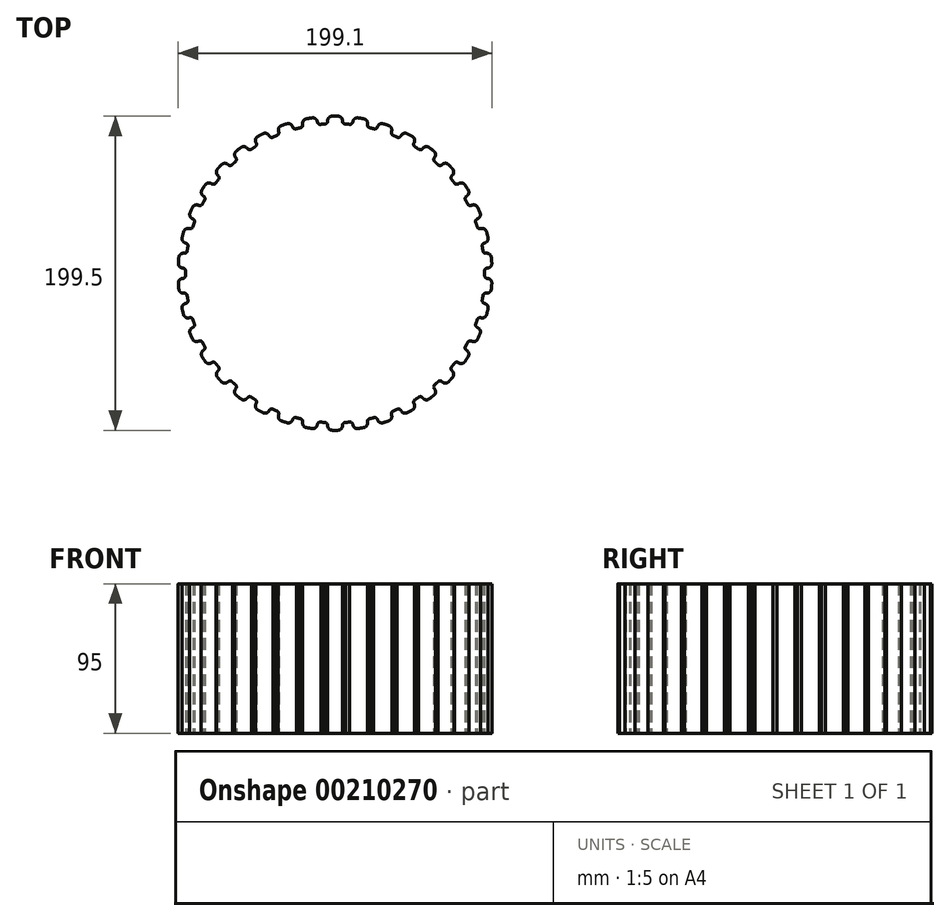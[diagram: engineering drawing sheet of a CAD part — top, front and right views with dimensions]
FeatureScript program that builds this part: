
annotation { "Feature Type Name" : "Feature", "Feature Type Description" : "" }
export const myFeature = defineFeature(function(context is Context, id is Id, definition is map)
    precondition{}
    {
        {
            var Q0;
            Q0=qCreatedBy(makeId("Top.planeOp"),FACE);
            var sketch = newSketch(context, id + "F0", { "sketchPlane" : qUnion([Q0])});
            skLineSegment(sketch, "E0", {"start": v(0, 0) * mm, "end": v(0, 110) * mm, "construction": true});
            skArc(sketch, "E1", {"start": v(2, 104.98) * mm, "mid": v(0, 105) * mm, "end": v(-2, 104.98) * mm});
            skArc(sketch, "E2.filletArc", {"start": v(-2, 104.98) * mm, "mid": v(-4.13, 104.03) * mm, "end": v(-4.94, 101.85) * mm});
            skArc(sketch, "E3.filletArc", {"start": v(4.94, 101.85) * mm, "mid": v(4.13, 104.03) * mm, "end": v(2, 104.98) * mm});
            skArc(sketch, "E4", {"start": v(-6.98, 99.76) * mm, "mid": v(-5.5, 100.36) * mm, "end": v(-4.94, 101.85) * mm});
            skLineSegment(sketch, "E5", {"start": v(-6.98, 99.76) * mm, "end": v(0, 0) * mm, "construction": true});
            skLineSegment(sketch, "E6", {"start": v(0, 0) * mm, "end": v(6.98, 99.76) * mm, "construction": true});
            skCircle(sketch, "E7", {"center": v(0, 0) * mm, "radius": 100 * mm});
            skArc(sketch, "E8", {"start": v(4.94, 101.85) * mm, "mid": v(5.5, 100.36) * mm, "end": v(6.98, 99.76) * mm});
            skArc(sketch, "E9.1.0", {"start": v(-23.3, 97.25) * mm, "mid": v(-21.95, 98.09) * mm, "end": v(-21.64, 99.64) * mm});
            skArc(sketch, "E9.1.1", {"start": v(-19.25, 103.22) * mm, "mid": v(-21.2, 101.93) * mm, "end": v(-21.64, 99.64) * mm});
            skArc(sketch, "E9.1.2", {"start": v(-15.3, 103.88) * mm, "mid": v(-17.28, 103.57) * mm, "end": v(-19.25, 103.22) * mm});
            skArc(sketch, "E9.1.3", {"start": v(-11.9, 101.27) * mm, "mid": v(-13.05, 103.3) * mm, "end": v(-15.3, 103.88) * mm});
            skArc(sketch, "E9.1.4", {"start": v(-11.9, 101.27) * mm, "mid": v(-11.09, 99.9) * mm, "end": v(-9.54, 99.54) * mm});
            skArc(sketch, "E9.2.0", {"start": v(-38.99, 92.09) * mm, "mid": v(-37.8, 93.14) * mm, "end": v(-37.74, 94.72) * mm});
            skArc(sketch, "E9.2.1", {"start": v(-35.98, 98.64) * mm, "mid": v(-37.69, 97.06) * mm, "end": v(-37.74, 94.72) * mm});
            skArc(sketch, "E9.2.2", {"start": v(-32.2, 99.94) * mm, "mid": v(-34.1, 99.31) * mm, "end": v(-35.98, 98.64) * mm});
            skArc(sketch, "E9.2.3", {"start": v(-28.4, 97.93) * mm, "mid": v(-29.87, 99.74) * mm, "end": v(-32.2, 99.94) * mm});
            skArc(sketch, "E9.2.4", {"start": v(-28.4, 97.93) * mm, "mid": v(-27.38, 96.71) * mm, "end": v(-25.8, 96.62) * mm});
            skArc(sketch, "E9.3.0", {"start": v(-53.61, 84.41) * mm, "mid": v(-52.6, 85.64) * mm, "end": v(-52.82, 87.22) * mm});
            skArc(sketch, "E9.3.1", {"start": v(-51.72, 91.38) * mm, "mid": v(-53.15, 89.53) * mm, "end": v(-52.82, 87.22) * mm});
            skArc(sketch, "E9.3.2", {"start": v(-48.2, 93.28) * mm, "mid": v(-49.97, 92.34) * mm, "end": v(-51.72, 91.38) * mm});
            skArc(sketch, "E9.3.3", {"start": v(-44.13, 91.92) * mm, "mid": v(-45.88, 93.46) * mm, "end": v(-48.2, 93.28) * mm});
            skArc(sketch, "E9.3.4", {"start": v(-44.13, 91.92) * mm, "mid": v(-42.92, 90.88) * mm, "end": v(-41.34, 91.05) * mm});
            skArc(sketch, "E9.4.0", {"start": v(-66.78, 74.44) * mm, "mid": v(-65.99, 75.82) * mm, "end": v(-66.45, 77.34) * mm});
            skArc(sketch, "E9.4.1", {"start": v(-66.06, 81.62) * mm, "mid": v(-67.16, 79.56) * mm, "end": v(-66.45, 77.34) * mm});
            skArc(sketch, "E9.4.2", {"start": v(-62.9, 84.07) * mm, "mid": v(-64.5, 82.86) * mm, "end": v(-66.06, 81.62) * mm});
            skArc(sketch, "E9.4.3", {"start": v(-58.66, 83.4) * mm, "mid": v(-60.64, 84.63) * mm, "end": v(-62.9, 84.07) * mm});
            skArc(sketch, "E9.4.4", {"start": v(-58.66, 83.4) * mm, "mid": v(-57.3, 82.58) * mm, "end": v(-55.77, 83) * mm});
            skArc(sketch, "E9.5.0", {"start": v(-78.12, 62.43) * mm, "mid": v(-77.57, 63.92) * mm, "end": v(-78.28, 65.34) * mm});
            skArc(sketch, "E9.5.1", {"start": v(-78.6, 69.63) * mm, "mid": v(-79.34, 67.42) * mm, "end": v(-78.28, 65.34) * mm});
            skArc(sketch, "E9.5.2", {"start": v(-75.88, 72.57) * mm, "mid": v(-77.25, 71.11) * mm, "end": v(-78.6, 69.63) * mm});
            skArc(sketch, "E9.5.3", {"start": v(-71.59, 72.61) * mm, "mid": v(-73.74, 73.5) * mm, "end": v(-75.88, 72.57) * mm});
            skArc(sketch, "E9.5.4", {"start": v(-71.59, 72.61) * mm, "mid": v(-70.1, 72.02) * mm, "end": v(-68.67, 72.7) * mm});
            skArc(sketch, "E9.6.0", {"start": v(-87.33, 48.72) * mm, "mid": v(-87.03, 50.28) * mm, "end": v(-87.96, 51.57) * mm});
            skArc(sketch, "E9.6.1", {"start": v(-88.98, 55.74) * mm, "mid": v(-89.35, 53.44) * mm, "end": v(-87.96, 51.57) * mm});
            skArc(sketch, "E9.6.2", {"start": v(-86.8, 59.1) * mm, "mid": v(-87.9, 57.43) * mm, "end": v(-88.98, 55.74) * mm});
            skArc(sketch, "E9.6.3", {"start": v(-82.56, 59.84) * mm, "mid": v(-84.83, 60.36) * mm, "end": v(-86.8, 59.1) * mm});
            skArc(sketch, "E9.6.4", {"start": v(-82.56, 59.84) * mm, "mid": v(-81, 59.5) * mm, "end": v(-79.7, 60.4) * mm});
            skArc(sketch, "E9.7.0", {"start": v(-94.16, 33.68) * mm, "mid": v(-94.12, 35.27) * mm, "end": v(-95.25, 36.39) * mm});
            skArc(sketch, "E9.7.1", {"start": v(-96.94, 40.34) * mm, "mid": v(-96.93, 38) * mm, "end": v(-95.25, 36.39) * mm});
            skArc(sketch, "E9.7.2", {"start": v(-95.34, 44) * mm, "mid": v(-96.16, 42.18) * mm, "end": v(-96.94, 40.34) * mm});
            skArc(sketch, "E9.7.3", {"start": v(-91.28, 45.43) * mm, "mid": v(-93.61, 45.57) * mm, "end": v(-95.34, 44) * mm});
            skArc(sketch, "E9.7.4", {"start": v(-91.28, 45.43) * mm, "mid": v(-89.7, 45.36) * mm, "end": v(-88.55, 46.46) * mm});
            skArc(sketch, "E9.8.0", {"start": v(-98.42, 17.73) * mm, "mid": v(-98.64, 19.3) * mm, "end": v(-99.94, 20.21) * mm});
            skArc(sketch, "E9.8.1", {"start": v(-102.26, 23.83) * mm, "mid": v(-101.86, 21.53) * mm, "end": v(-99.94, 20.21) * mm});
            skArc(sketch, "E9.8.2", {"start": v(-101.28, 27.71) * mm, "mid": v(-101.79, 25.78) * mm, "end": v(-102.26, 23.83) * mm});
            skArc(sketch, "E9.8.3", {"start": v(-97.52, 29.8) * mm, "mid": v(-99.84, 29.54) * mm, "end": v(-101.28, 27.71) * mm});
            skArc(sketch, "E9.8.4", {"start": v(-97.52, 29.8) * mm, "mid": v(-95.94, 29.97) * mm, "end": v(-95, 31.25) * mm});
            skArc(sketch, "E9.9.0", {"start": v(-100, 1.29) * mm, "mid": v(-100.47, 2.8) * mm, "end": v(-101.9, 3.49) * mm});
            skArc(sketch, "E9.9.1", {"start": v(-104.79, 6.68) * mm, "mid": v(-104.02, 4.47) * mm, "end": v(-101.9, 3.49) * mm});
            skArc(sketch, "E9.9.2", {"start": v(-104.46, 10.66) * mm, "mid": v(-104.64, 8.67) * mm, "end": v(-104.79, 6.68) * mm});
            skArc(sketch, "E9.9.3", {"start": v(-101.1, 13.33) * mm, "mid": v(-103.34, 12.7) * mm, "end": v(-104.46, 10.66) * mm});
            skArc(sketch, "E9.9.4", {"start": v(-101.1, 13.33) * mm, "mid": v(-99.56, 13.77) * mm, "end": v(-98.84, 15.19) * mm});
            skArc(sketch, "E9.10.0", {"start": v(-98.84, -15.19) * mm, "mid": v(-99.56, -13.77) * mm, "end": v(-101.1, -13.33) * mm});
            skArc(sketch, "E9.10.1", {"start": v(-104.46, -10.66) * mm, "mid": v(-103.34, -12.7) * mm, "end": v(-101.1, -13.33) * mm});
            skArc(sketch, "E9.10.2", {"start": v(-104.79, -6.68) * mm, "mid": v(-104.64, -8.67) * mm, "end": v(-104.46, -10.66) * mm});
            skArc(sketch, "E9.10.3", {"start": v(-101.9, -3.49) * mm, "mid": v(-104.02, -4.47) * mm, "end": v(-104.79, -6.68) * mm});
            skArc(sketch, "E9.10.4", {"start": v(-101.9, -3.49) * mm, "mid": v(-100.47, -2.8) * mm, "end": v(-100, -1.29) * mm});
            skArc(sketch, "E9.11.0", {"start": v(-95, -31.25) * mm, "mid": v(-95.94, -29.97) * mm, "end": v(-97.52, -29.8) * mm});
            skArc(sketch, "E9.11.1", {"start": v(-101.28, -27.71) * mm, "mid": v(-99.84, -29.54) * mm, "end": v(-97.52, -29.8) * mm});
            skArc(sketch, "E9.11.2", {"start": v(-102.26, -23.83) * mm, "mid": v(-101.79, -25.78) * mm, "end": v(-101.28, -27.71) * mm});
            skArc(sketch, "E9.11.3", {"start": v(-99.94, -20.21) * mm, "mid": v(-101.86, -21.53) * mm, "end": v(-102.26, -23.83) * mm});
            skArc(sketch, "E9.11.4", {"start": v(-99.94, -20.21) * mm, "mid": v(-98.64, -19.3) * mm, "end": v(-98.42, -17.73) * mm});
            skArc(sketch, "E9.12.0", {"start": v(-88.55, -46.46) * mm, "mid": v(-89.7, -45.36) * mm, "end": v(-91.28, -45.43) * mm});
            skArc(sketch, "E9.12.1", {"start": v(-95.34, -44) * mm, "mid": v(-93.61, -45.57) * mm, "end": v(-91.28, -45.43) * mm});
            skArc(sketch, "E9.12.2", {"start": v(-96.94, -40.34) * mm, "mid": v(-96.16, -42.18) * mm, "end": v(-95.34, -44) * mm});
            skArc(sketch, "E9.12.3", {"start": v(-95.25, -36.39) * mm, "mid": v(-96.93, -38) * mm, "end": v(-96.94, -40.34) * mm});
            skArc(sketch, "E9.12.4", {"start": v(-95.25, -36.39) * mm, "mid": v(-94.12, -35.27) * mm, "end": v(-94.16, -33.68) * mm});
            skArc(sketch, "E9.13.0", {"start": v(-79.7, -60.4) * mm, "mid": v(-81, -59.5) * mm, "end": v(-82.56, -59.84) * mm});
            skArc(sketch, "E9.13.1", {"start": v(-86.8, -59.1) * mm, "mid": v(-84.83, -60.36) * mm, "end": v(-82.56, -59.84) * mm});
            skArc(sketch, "E9.13.2", {"start": v(-88.98, -55.74) * mm, "mid": v(-87.9, -57.43) * mm, "end": v(-86.8, -59.1) * mm});
            skArc(sketch, "E9.13.3", {"start": v(-87.96, -51.57) * mm, "mid": v(-89.35, -53.44) * mm, "end": v(-88.98, -55.74) * mm});
            skArc(sketch, "E9.13.4", {"start": v(-87.96, -51.57) * mm, "mid": v(-87.03, -50.28) * mm, "end": v(-87.33, -48.72) * mm});
            skArc(sketch, "E9.14.0", {"start": v(-68.67, -72.7) * mm, "mid": v(-70.1, -72.02) * mm, "end": v(-71.59, -72.61) * mm});
            skArc(sketch, "E9.14.1", {"start": v(-75.88, -72.57) * mm, "mid": v(-73.74, -73.5) * mm, "end": v(-71.59, -72.61) * mm});
            skArc(sketch, "E9.14.2", {"start": v(-78.6, -69.63) * mm, "mid": v(-77.25, -71.11) * mm, "end": v(-75.88, -72.57) * mm});
            skArc(sketch, "E9.14.3", {"start": v(-78.28, -65.34) * mm, "mid": v(-79.34, -67.42) * mm, "end": v(-78.6, -69.63) * mm});
            skArc(sketch, "E9.14.4", {"start": v(-78.28, -65.34) * mm, "mid": v(-77.57, -63.92) * mm, "end": v(-78.12, -62.43) * mm});
            skArc(sketch, "E9.15.0", {"start": v(-55.77, -83) * mm, "mid": v(-57.3, -82.58) * mm, "end": v(-58.66, -83.4) * mm});
            skArc(sketch, "E9.15.1", {"start": v(-62.9, -84.07) * mm, "mid": v(-60.64, -84.63) * mm, "end": v(-58.66, -83.4) * mm});
            skArc(sketch, "E9.15.2", {"start": v(-66.06, -81.62) * mm, "mid": v(-64.5, -82.86) * mm, "end": v(-62.9, -84.07) * mm});
            skArc(sketch, "E9.15.3", {"start": v(-66.45, -77.34) * mm, "mid": v(-67.16, -79.56) * mm, "end": v(-66.06, -81.62) * mm});
            skArc(sketch, "E9.15.4", {"start": v(-66.45, -77.34) * mm, "mid": v(-65.99, -75.82) * mm, "end": v(-66.78, -74.44) * mm});
            skArc(sketch, "E9.16.0", {"start": v(-41.34, -91.05) * mm, "mid": v(-42.92, -90.88) * mm, "end": v(-44.13, -91.92) * mm});
            skArc(sketch, "E9.16.1", {"start": v(-48.2, -93.28) * mm, "mid": v(-45.88, -93.46) * mm, "end": v(-44.13, -91.92) * mm});
            skArc(sketch, "E9.16.2", {"start": v(-51.72, -91.38) * mm, "mid": v(-49.97, -92.34) * mm, "end": v(-48.2, -93.28) * mm});
            skArc(sketch, "E9.16.3", {"start": v(-52.82, -87.22) * mm, "mid": v(-53.15, -89.53) * mm, "end": v(-51.72, -91.38) * mm});
            skArc(sketch, "E9.16.4", {"start": v(-52.82, -87.22) * mm, "mid": v(-52.6, -85.64) * mm, "end": v(-53.61, -84.41) * mm});
            skArc(sketch, "E9.17.0", {"start": v(-25.8, -96.62) * mm, "mid": v(-27.38, -96.71) * mm, "end": v(-28.4, -97.93) * mm});
            skArc(sketch, "E9.17.1", {"start": v(-32.2, -99.94) * mm, "mid": v(-29.87, -99.74) * mm, "end": v(-28.4, -97.93) * mm});
            skArc(sketch, "E9.17.2", {"start": v(-35.98, -98.64) * mm, "mid": v(-34.1, -99.31) * mm, "end": v(-32.2, -99.94) * mm});
            skArc(sketch, "E9.17.3", {"start": v(-37.74, -94.72) * mm, "mid": v(-37.69, -97.06) * mm, "end": v(-35.98, -98.64) * mm});
            skArc(sketch, "E9.17.4", {"start": v(-37.74, -94.72) * mm, "mid": v(-37.8, -93.14) * mm, "end": v(-38.99, -92.09) * mm});
            skArc(sketch, "E9.18.0", {"start": v(-9.54, -99.54) * mm, "mid": v(-11.09, -99.9) * mm, "end": v(-11.9, -101.27) * mm});
            skArc(sketch, "E9.18.1", {"start": v(-15.3, -103.88) * mm, "mid": v(-13.05, -103.3) * mm, "end": v(-11.9, -101.27) * mm});
            skArc(sketch, "E9.18.2", {"start": v(-19.25, -103.22) * mm, "mid": v(-17.28, -103.57) * mm, "end": v(-15.3, -103.88) * mm});
            skArc(sketch, "E9.18.3", {"start": v(-21.64, -99.64) * mm, "mid": v(-21.2, -101.93) * mm, "end": v(-19.25, -103.22) * mm});
            skArc(sketch, "E9.18.4", {"start": v(-21.64, -99.64) * mm, "mid": v(-21.95, -98.09) * mm, "end": v(-23.3, -97.25) * mm});
            skArc(sketch, "E9.19.0", {"start": v(6.98, -99.76) * mm, "mid": v(5.5, -100.36) * mm, "end": v(4.94, -101.85) * mm});
            skArc(sketch, "E9.19.1", {"start": v(2, -104.98) * mm, "mid": v(4.13, -104.03) * mm, "end": v(4.94, -101.85) * mm});
            skArc(sketch, "E9.19.2", {"start": v(-2, -104.98) * mm, "mid": v(0, -105) * mm, "end": v(2, -104.98) * mm});
            skArc(sketch, "E9.19.3", {"start": v(-4.94, -101.85) * mm, "mid": v(-4.13, -104.03) * mm, "end": v(-2, -104.98) * mm});
            skArc(sketch, "E9.19.4", {"start": v(-4.94, -101.85) * mm, "mid": v(-5.5, -100.36) * mm, "end": v(-6.98, -99.76) * mm});
            skArc(sketch, "E9.20.0", {"start": v(23.3, -97.25) * mm, "mid": v(21.95, -98.09) * mm, "end": v(21.64, -99.64) * mm});
            skArc(sketch, "E9.20.1", {"start": v(19.25, -103.22) * mm, "mid": v(21.2, -101.93) * mm, "end": v(21.64, -99.64) * mm});
            skArc(sketch, "E9.20.2", {"start": v(15.3, -103.88) * mm, "mid": v(17.28, -103.57) * mm, "end": v(19.25, -103.22) * mm});
            skArc(sketch, "E9.20.3", {"start": v(11.9, -101.27) * mm, "mid": v(13.05, -103.3) * mm, "end": v(15.3, -103.88) * mm});
            skArc(sketch, "E9.20.4", {"start": v(11.9, -101.27) * mm, "mid": v(11.09, -99.9) * mm, "end": v(9.54, -99.54) * mm});
            skArc(sketch, "E9.21.0", {"start": v(38.99, -92.09) * mm, "mid": v(37.8, -93.14) * mm, "end": v(37.74, -94.72) * mm});
            skArc(sketch, "E9.21.1", {"start": v(35.98, -98.64) * mm, "mid": v(37.69, -97.06) * mm, "end": v(37.74, -94.72) * mm});
            skArc(sketch, "E9.21.2", {"start": v(32.2, -99.94) * mm, "mid": v(34.1, -99.31) * mm, "end": v(35.98, -98.64) * mm});
            skArc(sketch, "E9.21.3", {"start": v(28.4, -97.93) * mm, "mid": v(29.87, -99.74) * mm, "end": v(32.2, -99.94) * mm});
            skArc(sketch, "E9.21.4", {"start": v(28.4, -97.93) * mm, "mid": v(27.38, -96.71) * mm, "end": v(25.8, -96.62) * mm});
            skArc(sketch, "E9.22.0", {"start": v(53.61, -84.41) * mm, "mid": v(52.6, -85.64) * mm, "end": v(52.82, -87.22) * mm});
            skArc(sketch, "E9.22.1", {"start": v(51.72, -91.38) * mm, "mid": v(53.15, -89.53) * mm, "end": v(52.82, -87.22) * mm});
            skArc(sketch, "E9.22.2", {"start": v(48.2, -93.28) * mm, "mid": v(49.97, -92.34) * mm, "end": v(51.72, -91.38) * mm});
            skArc(sketch, "E9.22.3", {"start": v(44.13, -91.92) * mm, "mid": v(45.88, -93.46) * mm, "end": v(48.2, -93.28) * mm});
            skArc(sketch, "E9.22.4", {"start": v(44.13, -91.92) * mm, "mid": v(42.92, -90.88) * mm, "end": v(41.34, -91.05) * mm});
            skArc(sketch, "E9.23.0", {"start": v(66.78, -74.44) * mm, "mid": v(65.99, -75.82) * mm, "end": v(66.45, -77.34) * mm});
            skArc(sketch, "E9.23.1", {"start": v(66.06, -81.62) * mm, "mid": v(67.16, -79.56) * mm, "end": v(66.45, -77.34) * mm});
            skArc(sketch, "E9.23.2", {"start": v(62.9, -84.07) * mm, "mid": v(64.5, -82.86) * mm, "end": v(66.06, -81.62) * mm});
            skArc(sketch, "E9.23.3", {"start": v(58.66, -83.4) * mm, "mid": v(60.64, -84.63) * mm, "end": v(62.9, -84.07) * mm});
            skArc(sketch, "E9.23.4", {"start": v(58.66, -83.4) * mm, "mid": v(57.3, -82.58) * mm, "end": v(55.77, -83) * mm});
            skArc(sketch, "E9.24.0", {"start": v(78.12, -62.43) * mm, "mid": v(77.57, -63.92) * mm, "end": v(78.28, -65.34) * mm});
            skArc(sketch, "E9.24.1", {"start": v(78.6, -69.63) * mm, "mid": v(79.34, -67.42) * mm, "end": v(78.28, -65.34) * mm});
            skArc(sketch, "E9.24.2", {"start": v(75.88, -72.57) * mm, "mid": v(77.25, -71.11) * mm, "end": v(78.6, -69.63) * mm});
            skArc(sketch, "E9.24.3", {"start": v(71.59, -72.61) * mm, "mid": v(73.74, -73.5) * mm, "end": v(75.88, -72.57) * mm});
            skArc(sketch, "E9.24.4", {"start": v(71.59, -72.61) * mm, "mid": v(70.1, -72.02) * mm, "end": v(68.67, -72.7) * mm});
            skArc(sketch, "E9.25.0", {"start": v(87.33, -48.72) * mm, "mid": v(87.03, -50.28) * mm, "end": v(87.96, -51.57) * mm});
            skArc(sketch, "E9.25.1", {"start": v(88.98, -55.74) * mm, "mid": v(89.35, -53.44) * mm, "end": v(87.96, -51.57) * mm});
            skArc(sketch, "E9.25.2", {"start": v(86.8, -59.1) * mm, "mid": v(87.9, -57.43) * mm, "end": v(88.98, -55.74) * mm});
            skArc(sketch, "E9.25.3", {"start": v(82.56, -59.84) * mm, "mid": v(84.83, -60.36) * mm, "end": v(86.8, -59.1) * mm});
            skArc(sketch, "E9.25.4", {"start": v(82.56, -59.84) * mm, "mid": v(81, -59.5) * mm, "end": v(79.7, -60.4) * mm});
            skArc(sketch, "E9.26.0", {"start": v(94.16, -33.68) * mm, "mid": v(94.12, -35.27) * mm, "end": v(95.25, -36.39) * mm});
            skArc(sketch, "E9.26.1", {"start": v(96.94, -40.34) * mm, "mid": v(96.93, -38) * mm, "end": v(95.25, -36.39) * mm});
            skArc(sketch, "E9.26.2", {"start": v(95.34, -44) * mm, "mid": v(96.16, -42.18) * mm, "end": v(96.94, -40.34) * mm});
            skArc(sketch, "E9.26.3", {"start": v(91.28, -45.43) * mm, "mid": v(93.61, -45.57) * mm, "end": v(95.34, -44) * mm});
            skArc(sketch, "E9.26.4", {"start": v(91.28, -45.43) * mm, "mid": v(89.7, -45.36) * mm, "end": v(88.55, -46.46) * mm});
            skArc(sketch, "E9.27.0", {"start": v(98.42, -17.73) * mm, "mid": v(98.64, -19.3) * mm, "end": v(99.94, -20.21) * mm});
            skArc(sketch, "E9.27.1", {"start": v(102.26, -23.83) * mm, "mid": v(101.86, -21.53) * mm, "end": v(99.94, -20.21) * mm});
            skArc(sketch, "E9.27.2", {"start": v(101.28, -27.71) * mm, "mid": v(101.79, -25.78) * mm, "end": v(102.26, -23.83) * mm});
            skArc(sketch, "E9.27.3", {"start": v(97.52, -29.8) * mm, "mid": v(99.84, -29.54) * mm, "end": v(101.28, -27.71) * mm});
            skArc(sketch, "E9.27.4", {"start": v(97.52, -29.8) * mm, "mid": v(95.94, -29.97) * mm, "end": v(95, -31.25) * mm});
            skArc(sketch, "E9.28.0", {"start": v(100, -1.29) * mm, "mid": v(100.47, -2.8) * mm, "end": v(101.9, -3.49) * mm});
            skArc(sketch, "E9.28.1", {"start": v(104.79, -6.68) * mm, "mid": v(104.02, -4.47) * mm, "end": v(101.9, -3.49) * mm});
            skArc(sketch, "E9.28.2", {"start": v(104.46, -10.66) * mm, "mid": v(104.64, -8.67) * mm, "end": v(104.79, -6.68) * mm});
            skArc(sketch, "E9.28.3", {"start": v(101.1, -13.33) * mm, "mid": v(103.34, -12.7) * mm, "end": v(104.46, -10.66) * mm});
            skArc(sketch, "E9.28.4", {"start": v(101.1, -13.33) * mm, "mid": v(99.56, -13.77) * mm, "end": v(98.84, -15.19) * mm});
            skArc(sketch, "E9.29.0", {"start": v(98.84, 15.19) * mm, "mid": v(99.56, 13.77) * mm, "end": v(101.1, 13.33) * mm});
            skArc(sketch, "E9.29.1", {"start": v(104.46, 10.66) * mm, "mid": v(103.34, 12.7) * mm, "end": v(101.1, 13.33) * mm});
            skArc(sketch, "E9.29.2", {"start": v(104.79, 6.68) * mm, "mid": v(104.64, 8.67) * mm, "end": v(104.46, 10.66) * mm});
            skArc(sketch, "E9.29.3", {"start": v(101.9, 3.49) * mm, "mid": v(104.02, 4.47) * mm, "end": v(104.79, 6.68) * mm});
            skArc(sketch, "E9.29.4", {"start": v(101.9, 3.49) * mm, "mid": v(100.47, 2.8) * mm, "end": v(100, 1.29) * mm});
            skArc(sketch, "E9.30.0", {"start": v(95, 31.25) * mm, "mid": v(95.94, 29.97) * mm, "end": v(97.52, 29.8) * mm});
            skArc(sketch, "E9.30.1", {"start": v(101.28, 27.71) * mm, "mid": v(99.84, 29.54) * mm, "end": v(97.52, 29.8) * mm});
            skArc(sketch, "E9.30.2", {"start": v(102.26, 23.83) * mm, "mid": v(101.79, 25.78) * mm, "end": v(101.28, 27.71) * mm});
            skArc(sketch, "E9.30.3", {"start": v(99.94, 20.21) * mm, "mid": v(101.86, 21.53) * mm, "end": v(102.26, 23.83) * mm});
            skArc(sketch, "E9.30.4", {"start": v(99.94, 20.21) * mm, "mid": v(98.64, 19.3) * mm, "end": v(98.42, 17.73) * mm});
            skArc(sketch, "E9.31.0", {"start": v(88.55, 46.46) * mm, "mid": v(89.7, 45.36) * mm, "end": v(91.28, 45.43) * mm});
            skArc(sketch, "E9.31.1", {"start": v(95.34, 44) * mm, "mid": v(93.61, 45.57) * mm, "end": v(91.28, 45.43) * mm});
            skArc(sketch, "E9.31.2", {"start": v(96.94, 40.34) * mm, "mid": v(96.16, 42.18) * mm, "end": v(95.34, 44) * mm});
            skArc(sketch, "E9.31.3", {"start": v(95.25, 36.39) * mm, "mid": v(96.93, 38) * mm, "end": v(96.94, 40.34) * mm});
            skArc(sketch, "E9.31.4", {"start": v(95.25, 36.39) * mm, "mid": v(94.12, 35.27) * mm, "end": v(94.16, 33.68) * mm});
            skArc(sketch, "E9.32.0", {"start": v(79.7, 60.4) * mm, "mid": v(81, 59.5) * mm, "end": v(82.56, 59.84) * mm});
            skArc(sketch, "E9.32.1", {"start": v(86.8, 59.1) * mm, "mid": v(84.83, 60.36) * mm, "end": v(82.56, 59.84) * mm});
            skArc(sketch, "E9.32.2", {"start": v(88.98, 55.74) * mm, "mid": v(87.9, 57.43) * mm, "end": v(86.8, 59.1) * mm});
            skArc(sketch, "E9.32.3", {"start": v(87.96, 51.57) * mm, "mid": v(89.35, 53.44) * mm, "end": v(88.98, 55.74) * mm});
            skArc(sketch, "E9.32.4", {"start": v(87.96, 51.57) * mm, "mid": v(87.03, 50.28) * mm, "end": v(87.33, 48.72) * mm});
            skArc(sketch, "E9.33.0", {"start": v(68.67, 72.7) * mm, "mid": v(70.1, 72.02) * mm, "end": v(71.59, 72.61) * mm});
            skArc(sketch, "E9.33.1", {"start": v(75.88, 72.57) * mm, "mid": v(73.74, 73.5) * mm, "end": v(71.59, 72.61) * mm});
            skArc(sketch, "E9.33.2", {"start": v(78.6, 69.63) * mm, "mid": v(77.25, 71.11) * mm, "end": v(75.88, 72.57) * mm});
            skArc(sketch, "E9.33.3", {"start": v(78.28, 65.34) * mm, "mid": v(79.34, 67.42) * mm, "end": v(78.6, 69.63) * mm});
            skArc(sketch, "E9.33.4", {"start": v(78.28, 65.34) * mm, "mid": v(77.57, 63.92) * mm, "end": v(78.12, 62.43) * mm});
            skArc(sketch, "E9.34.0", {"start": v(55.77, 83) * mm, "mid": v(57.3, 82.58) * mm, "end": v(58.66, 83.4) * mm});
            skArc(sketch, "E9.34.1", {"start": v(62.9, 84.07) * mm, "mid": v(60.64, 84.63) * mm, "end": v(58.66, 83.4) * mm});
            skArc(sketch, "E9.34.2", {"start": v(66.06, 81.62) * mm, "mid": v(64.5, 82.86) * mm, "end": v(62.9, 84.07) * mm});
            skArc(sketch, "E9.34.3", {"start": v(66.45, 77.34) * mm, "mid": v(67.16, 79.56) * mm, "end": v(66.06, 81.62) * mm});
            skArc(sketch, "E9.34.4", {"start": v(66.45, 77.34) * mm, "mid": v(65.99, 75.82) * mm, "end": v(66.78, 74.44) * mm});
            skArc(sketch, "E9.35.0", {"start": v(41.34, 91.05) * mm, "mid": v(42.92, 90.88) * mm, "end": v(44.13, 91.92) * mm});
            skArc(sketch, "E9.35.1", {"start": v(48.2, 93.28) * mm, "mid": v(45.88, 93.46) * mm, "end": v(44.13, 91.92) * mm});
            skArc(sketch, "E9.35.2", {"start": v(51.72, 91.38) * mm, "mid": v(49.97, 92.34) * mm, "end": v(48.2, 93.28) * mm});
            skArc(sketch, "E9.35.3", {"start": v(52.82, 87.22) * mm, "mid": v(53.15, 89.53) * mm, "end": v(51.72, 91.38) * mm});
            skArc(sketch, "E9.35.4", {"start": v(52.82, 87.22) * mm, "mid": v(52.6, 85.64) * mm, "end": v(53.61, 84.41) * mm});
            skArc(sketch, "E9.36.0", {"start": v(25.8, 96.62) * mm, "mid": v(27.38, 96.71) * mm, "end": v(28.4, 97.93) * mm});
            skArc(sketch, "E9.36.1", {"start": v(32.2, 99.94) * mm, "mid": v(29.87, 99.74) * mm, "end": v(28.4, 97.93) * mm});
            skArc(sketch, "E9.36.2", {"start": v(35.98, 98.64) * mm, "mid": v(34.1, 99.31) * mm, "end": v(32.2, 99.94) * mm});
            skArc(sketch, "E9.36.3", {"start": v(37.74, 94.72) * mm, "mid": v(37.69, 97.06) * mm, "end": v(35.98, 98.64) * mm});
            skArc(sketch, "E9.36.4", {"start": v(37.74, 94.72) * mm, "mid": v(37.8, 93.14) * mm, "end": v(38.99, 92.09) * mm});
            skArc(sketch, "E9.37.0", {"start": v(9.54, 99.54) * mm, "mid": v(11.09, 99.9) * mm, "end": v(11.9, 101.27) * mm});
            skArc(sketch, "E9.37.1", {"start": v(15.3, 103.88) * mm, "mid": v(13.05, 103.3) * mm, "end": v(11.9, 101.27) * mm});
            skArc(sketch, "E9.37.2", {"start": v(19.25, 103.22) * mm, "mid": v(17.28, 103.57) * mm, "end": v(15.3, 103.88) * mm});
            skArc(sketch, "E9.37.3", {"start": v(21.64, 99.64) * mm, "mid": v(21.2, 101.93) * mm, "end": v(19.25, 103.22) * mm});
            skArc(sketch, "E9.37.4", {"start": v(21.64, 99.64) * mm, "mid": v(21.95, 98.09) * mm, "end": v(23.3, 97.25) * mm});
            skSolve(sketch);
        }
        {
            var Q0;
            {var subQ0=sQuery(id+"F0.wireOp",EDGE,"E9.3.1");Q0=makeQuery(id+"F0.imprint","IMPRINT",FACE,{"disambiguationData":[TD([[makeQuery(id+"F0.imprint","IMPRINT",EDGE,{"derivedFrom":subQ0}),1.0]])]});}
            var Q1;
            {var subQ0=sQuery(id+"F0.wireOp",EDGE,"E9.2.1");Q1=makeQuery(id+"F0.imprint","IMPRINT",FACE,{"disambiguationData":[TD([[makeQuery(id+"F0.imprint","IMPRINT",EDGE,{"derivedFrom":subQ0}),1.0]])]});}
            var Q2;
            {var subQ0=sQuery(id+"F0.wireOp",EDGE,"E9.1.1");Q2=makeQuery(id+"F0.imprint","IMPRINT",FACE,{"disambiguationData":[TD([[makeQuery(id+"F0.imprint","IMPRINT",EDGE,{"derivedFrom":subQ0}),1.0]])]});}
            var Q3;
            Q3=makeQuery(id+"F0.imprint","IMPRINT",FACE,{"disambiguationData":[TD([[makeQuery(id+"F0.imprint","IMPRINT",EDGE,{"derivedFrom":sQuery(id+"F0.wireOp",EDGE,"E1")}),1.0]])]});
            var Q4;
            {var subQ1=sQuery(id+"F0.wireOp",EDGE,"E9.37.1");Q4=makeQuery(id+"F0.imprint","IMPRINT",FACE,{"disambiguationData":[TD([[makeQuery(id+"F0.imprint","IMPRINT",EDGE,{"derivedFrom":subQ1}),1.0]])]});}
            var Q5;
            {var subQ0=sQuery(id+"F0.wireOp",EDGE,"E9.36.1");Q5=makeQuery(id+"F0.imprint","IMPRINT",FACE,{"disambiguationData":[TD([[makeQuery(id+"F0.imprint","IMPRINT",EDGE,{"derivedFrom":subQ0}),1.0]])]});}
            var Q6;
            {var subQ0=sQuery(id+"F0.wireOp",EDGE,"E9.35.1");Q6=makeQuery(id+"F0.imprint","IMPRINT",FACE,{"disambiguationData":[TD([[makeQuery(id+"F0.imprint","IMPRINT",EDGE,{"derivedFrom":subQ0}),1.0]])]});}
            var Q7;
            {var subQ0=sQuery(id+"F0.wireOp",EDGE,"E9.34.1");Q7=makeQuery(id+"F0.imprint","IMPRINT",FACE,{"disambiguationData":[TD([[makeQuery(id+"F0.imprint","IMPRINT",EDGE,{"derivedFrom":subQ0}),1.0]])]});}
            var Q8;
            {var subQ0=sQuery(id+"F0.wireOp",EDGE,"E9.33.1");Q8=makeQuery(id+"F0.imprint","IMPRINT",FACE,{"disambiguationData":[TD([[makeQuery(id+"F0.imprint","IMPRINT",EDGE,{"derivedFrom":subQ0}),1.0]])]});}
            var Q9;
            {var subQ0=sQuery(id+"F0.wireOp",EDGE,"E9.32.1");Q9=makeQuery(id+"F0.imprint","IMPRINT",FACE,{"disambiguationData":[TD([[makeQuery(id+"F0.imprint","IMPRINT",EDGE,{"derivedFrom":subQ0}),1.0]])]});}
            var Q10;
            {var subQ0=sQuery(id+"F0.wireOp",EDGE,"E9.31.1");Q10=makeQuery(id+"F0.imprint","IMPRINT",FACE,{"disambiguationData":[TD([[makeQuery(id+"F0.imprint","IMPRINT",EDGE,{"derivedFrom":subQ0}),1.0]])]});}
            var Q11;
            {var subQ5=sQuery(id+"F0.wireOp",EDGE,"E9.30.1");Q11=makeQuery(id+"F0.imprint","IMPRINT",FACE,{"disambiguationData":[TD([[makeQuery(id+"F0.imprint","IMPRINT",EDGE,{"derivedFrom":subQ5}),1.0]])]});}
            var Q12;
            {var subQ5=sQuery(id+"F0.wireOp",EDGE,"E9.4.1");Q12=makeQuery(id+"F0.imprint","IMPRINT",FACE,{"disambiguationData":[TD([[makeQuery(id+"F0.imprint","IMPRINT",EDGE,{"derivedFrom":subQ5}),1.0]])]});}
            var Q13;
            {var subQ0=sQuery(id+"F0.wireOp",EDGE,"E9.5.1");Q13=makeQuery(id+"F0.imprint","IMPRINT",FACE,{"disambiguationData":[TD([[makeQuery(id+"F0.imprint","IMPRINT",EDGE,{"derivedFrom":subQ0}),1.0]])]});}
            var Q14;
            {var subQ0=sQuery(id+"F0.wireOp",EDGE,"E9.6.1");Q14=makeQuery(id+"F0.imprint","IMPRINT",FACE,{"disambiguationData":[TD([[makeQuery(id+"F0.imprint","IMPRINT",EDGE,{"derivedFrom":subQ0}),1.0]])]});}
            var Q15;
            {var subQ0=sQuery(id+"F0.wireOp",EDGE,"E9.7.1");Q15=makeQuery(id+"F0.imprint","IMPRINT",FACE,{"disambiguationData":[TD([[makeQuery(id+"F0.imprint","IMPRINT",EDGE,{"derivedFrom":subQ0}),1.0]])]});}
            var Q16;
            {var subQ0=sQuery(id+"F0.wireOp",EDGE,"E9.8.1");Q16=makeQuery(id+"F0.imprint","IMPRINT",FACE,{"disambiguationData":[TD([[makeQuery(id+"F0.imprint","IMPRINT",EDGE,{"derivedFrom":subQ0}),1.0]])]});}
            var Q17;
            {var subQ1=sQuery(id+"F0.wireOp",EDGE,"E9.9.1");Q17=makeQuery(id+"F0.imprint","IMPRINT",FACE,{"disambiguationData":[TD([[makeQuery(id+"F0.imprint","IMPRINT",EDGE,{"derivedFrom":subQ1}),1.0]])]});}
            var Q18;
            {var subQ0=sQuery(id+"F0.wireOp",EDGE,"E9.10.1");Q18=makeQuery(id+"F0.imprint","IMPRINT",FACE,{"disambiguationData":[TD([[makeQuery(id+"F0.imprint","IMPRINT",EDGE,{"derivedFrom":subQ0}),1.0]])]});}
            var Q19;
            {var subQ0=sQuery(id+"F0.wireOp",EDGE,"E9.11.1");Q19=makeQuery(id+"F0.imprint","IMPRINT",FACE,{"disambiguationData":[TD([[makeQuery(id+"F0.imprint","IMPRINT",EDGE,{"derivedFrom":subQ0}),1.0]])]});}
            var Q20;
            {var subQ0=sQuery(id+"F0.wireOp",EDGE,"E9.12.1");Q20=makeQuery(id+"F0.imprint","IMPRINT",FACE,{"disambiguationData":[TD([[makeQuery(id+"F0.imprint","IMPRINT",EDGE,{"derivedFrom":subQ0}),1.0]])]});}
            var Q21;
            {var subQ0=sQuery(id+"F0.wireOp",EDGE,"E9.13.1");Q21=makeQuery(id+"F0.imprint","IMPRINT",FACE,{"disambiguationData":[TD([[makeQuery(id+"F0.imprint","IMPRINT",EDGE,{"derivedFrom":subQ0}),1.0]])]});}
            var Q22;
            {var subQ0=sQuery(id+"F0.wireOp",EDGE,"E9.14.1");Q22=makeQuery(id+"F0.imprint","IMPRINT",FACE,{"disambiguationData":[TD([[makeQuery(id+"F0.imprint","IMPRINT",EDGE,{"derivedFrom":subQ0}),1.0]])]});}
            var Q23;
            {var subQ0=sQuery(id+"F0.wireOp",EDGE,"E9.15.1");Q23=makeQuery(id+"F0.imprint","IMPRINT",FACE,{"disambiguationData":[TD([[makeQuery(id+"F0.imprint","IMPRINT",EDGE,{"derivedFrom":subQ0}),1.0]])]});}
            var Q24;
            {var subQ0=sQuery(id+"F0.wireOp",EDGE,"E9.16.1");Q24=makeQuery(id+"F0.imprint","IMPRINT",FACE,{"disambiguationData":[TD([[makeQuery(id+"F0.imprint","IMPRINT",EDGE,{"derivedFrom":subQ0}),1.0]])]});}
            var Q25;
            {var subQ0=sQuery(id+"F0.wireOp",EDGE,"E9.17.1");Q25=makeQuery(id+"F0.imprint","IMPRINT",FACE,{"disambiguationData":[TD([[makeQuery(id+"F0.imprint","IMPRINT",EDGE,{"derivedFrom":subQ0}),1.0]])]});}
            var Q26;
            {var subQ0=sQuery(id+"F0.wireOp",EDGE,"E9.18.1");Q26=makeQuery(id+"F0.imprint","IMPRINT",FACE,{"disambiguationData":[TD([[makeQuery(id+"F0.imprint","IMPRINT",EDGE,{"derivedFrom":subQ0}),1.0]])]});}
            var Q27;
            {var subQ0=sQuery(id+"F0.wireOp",EDGE,"E9.19.1");Q27=makeQuery(id+"F0.imprint","IMPRINT",FACE,{"disambiguationData":[TD([[makeQuery(id+"F0.imprint","IMPRINT",EDGE,{"derivedFrom":subQ0}),1.0]])]});}
            var Q28;
            {var subQ0=sQuery(id+"F0.wireOp",EDGE,"E9.20.1");Q28=makeQuery(id+"F0.imprint","IMPRINT",FACE,{"disambiguationData":[TD([[makeQuery(id+"F0.imprint","IMPRINT",EDGE,{"derivedFrom":subQ0}),1.0]])]});}
            var Q29;
            {var subQ0=sQuery(id+"F0.wireOp",EDGE,"E9.21.1");Q29=makeQuery(id+"F0.imprint","IMPRINT",FACE,{"disambiguationData":[TD([[makeQuery(id+"F0.imprint","IMPRINT",EDGE,{"derivedFrom":subQ0}),1.0]])]});}
            var Q30;
            {var subQ0=sQuery(id+"F0.wireOp",EDGE,"E9.22.1");Q30=makeQuery(id+"F0.imprint","IMPRINT",FACE,{"disambiguationData":[TD([[makeQuery(id+"F0.imprint","IMPRINT",EDGE,{"derivedFrom":subQ0}),1.0]])]});}
            var Q31;
            {var subQ0=sQuery(id+"F0.wireOp",EDGE,"E9.23.1");Q31=makeQuery(id+"F0.imprint","IMPRINT",FACE,{"disambiguationData":[TD([[makeQuery(id+"F0.imprint","IMPRINT",EDGE,{"derivedFrom":subQ0}),1.0]])]});}
            var Q32;
            {var subQ1=sQuery(id+"F0.wireOp",EDGE,"E9.24.1");Q32=makeQuery(id+"F0.imprint","IMPRINT",FACE,{"disambiguationData":[TD([[makeQuery(id+"F0.imprint","IMPRINT",EDGE,{"derivedFrom":subQ1}),1.0]])]});}
            var Q33;
            {var subQ0=sQuery(id+"F0.wireOp",EDGE,"E9.25.1");Q33=makeQuery(id+"F0.imprint","IMPRINT",FACE,{"disambiguationData":[TD([[makeQuery(id+"F0.imprint","IMPRINT",EDGE,{"derivedFrom":subQ0}),1.0]])]});}
            var Q34;
            {var subQ0=sQuery(id+"F0.wireOp",EDGE,"E9.26.1");Q34=makeQuery(id+"F0.imprint","IMPRINT",FACE,{"disambiguationData":[TD([[makeQuery(id+"F0.imprint","IMPRINT",EDGE,{"derivedFrom":subQ0}),1.0]])]});}
            var Q35;
            {var subQ0=sQuery(id+"F0.wireOp",EDGE,"E9.27.1");Q35=makeQuery(id+"F0.imprint","IMPRINT",FACE,{"disambiguationData":[TD([[makeQuery(id+"F0.imprint","IMPRINT",EDGE,{"derivedFrom":subQ0}),1.0]])]});}
            var Q36;
            {var subQ0=sQuery(id+"F0.wireOp",EDGE,"E9.28.1");Q36=makeQuery(id+"F0.imprint","IMPRINT",FACE,{"disambiguationData":[TD([[makeQuery(id+"F0.imprint","IMPRINT",EDGE,{"derivedFrom":subQ0}),1.0]])]});}
            var Q37;
            {var subQ0=sQuery(id+"F0.wireOp",EDGE,"E9.29.1");Q37=makeQuery(id+"F0.imprint","IMPRINT",FACE,{"disambiguationData":[TD([[makeQuery(id+"F0.imprint","IMPRINT",EDGE,{"derivedFrom":subQ0}),1.0]])]});}
            var Q38;
            {var subQ1=sQuery(id+"F0.wireOp",EDGE,"E7");var subQ176=sQuery(id+"F0.wireOp",EDGE,"E4");var subQ177=makeQuery(id+"F0.imprint","INTERSECT",VERTEX,{"disambiguationData":[OD(0.0)],"derivedFrom":[subQ176,subQ1]});Q38=makeQuery(id+"F0.imprint","IMPRINT",FACE,{"disambiguationData":[TD([[makeQuery(id+"F0.imprint","IMPRINT",EDGE,{"disambiguationData":[TD([[subQ177,-1.0]])],"derivedFrom":subQ176}),-1.0]])]});}
            extrude(context, id + "F1", {"entities" : qUnion([Q0, Q1, Q2, Q3, Q4, Q5, Q6, Q7, Q8, Q9, Q10, Q11, Q12, Q13, Q14, Q15, Q16, Q17, Q18, Q19, Q20, Q21, Q22, Q23, Q24, Q25, Q26, Q27, Q28, Q29, Q30, Q31, Q32, Q33, Q34, Q35, Q36, Q37, Q38]), "depth" : 100 * mm});
        }
        {
            var Q0;
            Q0=makeQuery(id+"F1.opExtrude","SWEPT_BODY",BODY,{"disambiguationData":[OSD([sQuery(id+"F0.wireOp",EDGE,"E1"),sQuery(id+"F0.wireOp",EDGE,"E2.filletArc"),sQuery(id+"F0.wireOp",EDGE,"E3.filletArc"),sQuery(id+"F0.wireOp",EDGE,"E4"),sQuery(id+"F0.wireOp",EDGE,"E7"),sQuery(id+"F0.wireOp",EDGE,"E8"),sQuery(id+"F0.wireOp",EDGE,"E9.1.0"),sQuery(id+"F0.wireOp",EDGE,"E9.1.1"),sQuery(id+"F0.wireOp",EDGE,"E9.1.2"),sQuery(id+"F0.wireOp",EDGE,"E9.1.3"),sQuery(id+"F0.wireOp",EDGE,"E9.1.4"),sQuery(id+"F0.wireOp",EDGE,"E9.2.0"),sQuery(id+"F0.wireOp",EDGE,"E9.2.1"),sQuery(id+"F0.wireOp",EDGE,"E9.2.2"),sQuery(id+"F0.wireOp",EDGE,"E9.2.3"),sQuery(id+"F0.wireOp",EDGE,"E9.2.4"),sQuery(id+"F0.wireOp",EDGE,"E9.3.0"),sQuery(id+"F0.wireOp",EDGE,"E9.3.1"),sQuery(id+"F0.wireOp",EDGE,"E9.3.2"),sQuery(id+"F0.wireOp",EDGE,"E9.3.3"),sQuery(id+"F0.wireOp",EDGE,"E9.3.4"),sQuery(id+"F0.wireOp",EDGE,"E9.4.0"),sQuery(id+"F0.wireOp",EDGE,"E9.4.1"),sQuery(id+"F0.wireOp",EDGE,"E9.4.2"),sQuery(id+"F0.wireOp",EDGE,"E9.4.3"),sQuery(id+"F0.wireOp",EDGE,"E9.4.4"),sQuery(id+"F0.wireOp",EDGE,"E9.5.0"),sQuery(id+"F0.wireOp",EDGE,"E9.5.1"),sQuery(id+"F0.wireOp",EDGE,"E9.5.2"),sQuery(id+"F0.wireOp",EDGE,"E9.5.3"),sQuery(id+"F0.wireOp",EDGE,"E9.5.4"),sQuery(id+"F0.wireOp",EDGE,"E9.6.0"),sQuery(id+"F0.wireOp",EDGE,"E9.6.1"),sQuery(id+"F0.wireOp",EDGE,"E9.6.2"),sQuery(id+"F0.wireOp",EDGE,"E9.6.3"),sQuery(id+"F0.wireOp",EDGE,"E9.6.4"),sQuery(id+"F0.wireOp",EDGE,"E9.7.0"),sQuery(id+"F0.wireOp",EDGE,"E9.7.1"),sQuery(id+"F0.wireOp",EDGE,"E9.7.2"),sQuery(id+"F0.wireOp",EDGE,"E9.7.3"),sQuery(id+"F0.wireOp",EDGE,"E9.7.4"),sQuery(id+"F0.wireOp",EDGE,"E9.8.0"),sQuery(id+"F0.wireOp",EDGE,"E9.8.1"),sQuery(id+"F0.wireOp",EDGE,"E9.8.2"),sQuery(id+"F0.wireOp",EDGE,"E9.8.3"),sQuery(id+"F0.wireOp",EDGE,"E9.8.4"),sQuery(id+"F0.wireOp",EDGE,"E9.9.0"),sQuery(id+"F0.wireOp",EDGE,"E9.9.1"),sQuery(id+"F0.wireOp",EDGE,"E9.9.2"),sQuery(id+"F0.wireOp",EDGE,"E9.9.3"),sQuery(id+"F0.wireOp",EDGE,"E9.9.4"),sQuery(id+"F0.wireOp",EDGE,"E9.10.0"),sQuery(id+"F0.wireOp",EDGE,"E9.10.1"),sQuery(id+"F0.wireOp",EDGE,"E9.10.2"),sQuery(id+"F0.wireOp",EDGE,"E9.10.3"),sQuery(id+"F0.wireOp",EDGE,"E9.10.4"),sQuery(id+"F0.wireOp",EDGE,"E9.11.0"),sQuery(id+"F0.wireOp",EDGE,"E9.11.1"),sQuery(id+"F0.wireOp",EDGE,"E9.11.2"),sQuery(id+"F0.wireOp",EDGE,"E9.11.3"),sQuery(id+"F0.wireOp",EDGE,"E9.11.4"),sQuery(id+"F0.wireOp",EDGE,"E9.12.0"),sQuery(id+"F0.wireOp",EDGE,"E9.12.1"),sQuery(id+"F0.wireOp",EDGE,"E9.12.2"),sQuery(id+"F0.wireOp",EDGE,"E9.12.3"),sQuery(id+"F0.wireOp",EDGE,"E9.12.4"),sQuery(id+"F0.wireOp",EDGE,"E9.13.0"),sQuery(id+"F0.wireOp",EDGE,"E9.13.1"),sQuery(id+"F0.wireOp",EDGE,"E9.13.2"),sQuery(id+"F0.wireOp",EDGE,"E9.13.3"),sQuery(id+"F0.wireOp",EDGE,"E9.13.4"),sQuery(id+"F0.wireOp",EDGE,"E9.14.0"),sQuery(id+"F0.wireOp",EDGE,"E9.14.1"),sQuery(id+"F0.wireOp",EDGE,"E9.14.2"),sQuery(id+"F0.wireOp",EDGE,"E9.14.3"),sQuery(id+"F0.wireOp",EDGE,"E9.14.4"),sQuery(id+"F0.wireOp",EDGE,"E9.15.0"),sQuery(id+"F0.wireOp",EDGE,"E9.15.1"),sQuery(id+"F0.wireOp",EDGE,"E9.15.2"),sQuery(id+"F0.wireOp",EDGE,"E9.15.3"),sQuery(id+"F0.wireOp",EDGE,"E9.15.4"),sQuery(id+"F0.wireOp",EDGE,"E9.16.0"),sQuery(id+"F0.wireOp",EDGE,"E9.16.1"),sQuery(id+"F0.wireOp",EDGE,"E9.16.2"),sQuery(id+"F0.wireOp",EDGE,"E9.16.3"),sQuery(id+"F0.wireOp",EDGE,"E9.16.4"),sQuery(id+"F0.wireOp",EDGE,"E9.17.0"),sQuery(id+"F0.wireOp",EDGE,"E9.17.1"),sQuery(id+"F0.wireOp",EDGE,"E9.17.2"),sQuery(id+"F0.wireOp",EDGE,"E9.17.3"),sQuery(id+"F0.wireOp",EDGE,"E9.17.4"),sQuery(id+"F0.wireOp",EDGE,"E9.18.0"),sQuery(id+"F0.wireOp",EDGE,"E9.18.1"),sQuery(id+"F0.wireOp",EDGE,"E9.18.2"),sQuery(id+"F0.wireOp",EDGE,"E9.18.3"),sQuery(id+"F0.wireOp",EDGE,"E9.18.4"),sQuery(id+"F0.wireOp",EDGE,"E9.19.0"),sQuery(id+"F0.wireOp",EDGE,"E9.19.1"),sQuery(id+"F0.wireOp",EDGE,"E9.19.2"),sQuery(id+"F0.wireOp",EDGE,"E9.19.3"),sQuery(id+"F0.wireOp",EDGE,"E9.19.4"),sQuery(id+"F0.wireOp",EDGE,"E9.20.0"),sQuery(id+"F0.wireOp",EDGE,"E9.20.1"),sQuery(id+"F0.wireOp",EDGE,"E9.20.2"),sQuery(id+"F0.wireOp",EDGE,"E9.20.3"),sQuery(id+"F0.wireOp",EDGE,"E9.20.4"),sQuery(id+"F0.wireOp",EDGE,"E9.21.0"),sQuery(id+"F0.wireOp",EDGE,"E9.21.1"),sQuery(id+"F0.wireOp",EDGE,"E9.21.2"),sQuery(id+"F0.wireOp",EDGE,"E9.21.3"),sQuery(id+"F0.wireOp",EDGE,"E9.21.4"),sQuery(id+"F0.wireOp",EDGE,"E9.22.0"),sQuery(id+"F0.wireOp",EDGE,"E9.22.1"),sQuery(id+"F0.wireOp",EDGE,"E9.22.2"),sQuery(id+"F0.wireOp",EDGE,"E9.22.3"),sQuery(id+"F0.wireOp",EDGE,"E9.22.4"),sQuery(id+"F0.wireOp",EDGE,"E9.23.0"),sQuery(id+"F0.wireOp",EDGE,"E9.23.1"),sQuery(id+"F0.wireOp",EDGE,"E9.23.2"),sQuery(id+"F0.wireOp",EDGE,"E9.23.3"),sQuery(id+"F0.wireOp",EDGE,"E9.23.4"),sQuery(id+"F0.wireOp",EDGE,"E9.24.0"),sQuery(id+"F0.wireOp",EDGE,"E9.24.1"),sQuery(id+"F0.wireOp",EDGE,"E9.24.2"),sQuery(id+"F0.wireOp",EDGE,"E9.24.3"),sQuery(id+"F0.wireOp",EDGE,"E9.24.4"),sQuery(id+"F0.wireOp",EDGE,"E9.25.0"),sQuery(id+"F0.wireOp",EDGE,"E9.25.1"),sQuery(id+"F0.wireOp",EDGE,"E9.25.2"),sQuery(id+"F0.wireOp",EDGE,"E9.25.3"),sQuery(id+"F0.wireOp",EDGE,"E9.25.4"),sQuery(id+"F0.wireOp",EDGE,"E9.26.0"),sQuery(id+"F0.wireOp",EDGE,"E9.26.1"),sQuery(id+"F0.wireOp",EDGE,"E9.26.2"),sQuery(id+"F0.wireOp",EDGE,"E9.26.3"),sQuery(id+"F0.wireOp",EDGE,"E9.26.4"),sQuery(id+"F0.wireOp",EDGE,"E9.27.0"),sQuery(id+"F0.wireOp",EDGE,"E9.27.1"),sQuery(id+"F0.wireOp",EDGE,"E9.27.2"),sQuery(id+"F0.wireOp",EDGE,"E9.27.3"),sQuery(id+"F0.wireOp",EDGE,"E9.27.4"),sQuery(id+"F0.wireOp",EDGE,"E9.28.0"),sQuery(id+"F0.wireOp",EDGE,"E9.28.1"),sQuery(id+"F0.wireOp",EDGE,"E9.28.2"),sQuery(id+"F0.wireOp",EDGE,"E9.28.3"),sQuery(id+"F0.wireOp",EDGE,"E9.28.4"),sQuery(id+"F0.wireOp",EDGE,"E9.29.0"),sQuery(id+"F0.wireOp",EDGE,"E9.29.1"),sQuery(id+"F0.wireOp",EDGE,"E9.29.2"),sQuery(id+"F0.wireOp",EDGE,"E9.29.3"),sQuery(id+"F0.wireOp",EDGE,"E9.29.4"),sQuery(id+"F0.wireOp",EDGE,"E9.30.0"),sQuery(id+"F0.wireOp",EDGE,"E9.30.1"),sQuery(id+"F0.wireOp",EDGE,"E9.30.2"),sQuery(id+"F0.wireOp",EDGE,"E9.30.3"),sQuery(id+"F0.wireOp",EDGE,"E9.30.4"),sQuery(id+"F0.wireOp",EDGE,"E9.31.0"),sQuery(id+"F0.wireOp",EDGE,"E9.31.1"),sQuery(id+"F0.wireOp",EDGE,"E9.31.2"),sQuery(id+"F0.wireOp",EDGE,"E9.31.3"),sQuery(id+"F0.wireOp",EDGE,"E9.31.4"),sQuery(id+"F0.wireOp",EDGE,"E9.32.0"),sQuery(id+"F0.wireOp",EDGE,"E9.32.1"),sQuery(id+"F0.wireOp",EDGE,"E9.32.2"),sQuery(id+"F0.wireOp",EDGE,"E9.32.3"),sQuery(id+"F0.wireOp",EDGE,"E9.32.4"),sQuery(id+"F0.wireOp",EDGE,"E9.33.0"),sQuery(id+"F0.wireOp",EDGE,"E9.33.1"),sQuery(id+"F0.wireOp",EDGE,"E9.33.2"),sQuery(id+"F0.wireOp",EDGE,"E9.33.3"),sQuery(id+"F0.wireOp",EDGE,"E9.33.4"),sQuery(id+"F0.wireOp",EDGE,"E9.34.0"),sQuery(id+"F0.wireOp",EDGE,"E9.34.1"),sQuery(id+"F0.wireOp",EDGE,"E9.34.2"),sQuery(id+"F0.wireOp",EDGE,"E9.34.3"),sQuery(id+"F0.wireOp",EDGE,"E9.34.4"),sQuery(id+"F0.wireOp",EDGE,"E9.35.0"),sQuery(id+"F0.wireOp",EDGE,"E9.35.1"),sQuery(id+"F0.wireOp",EDGE,"E9.35.2"),sQuery(id+"F0.wireOp",EDGE,"E9.35.3"),sQuery(id+"F0.wireOp",EDGE,"E9.35.4"),sQuery(id+"F0.wireOp",EDGE,"E9.36.0"),sQuery(id+"F0.wireOp",EDGE,"E9.36.1"),sQuery(id+"F0.wireOp",EDGE,"E9.36.2"),sQuery(id+"F0.wireOp",EDGE,"E9.36.3"),sQuery(id+"F0.wireOp",EDGE,"E9.36.4"),sQuery(id+"F0.wireOp",EDGE,"E9.37.0"),sQuery(id+"F0.wireOp",EDGE,"E9.37.1"),sQuery(id+"F0.wireOp",EDGE,"E9.37.2"),sQuery(id+"F0.wireOp",EDGE,"E9.37.3"),sQuery(id+"F0.wireOp",EDGE,"E9.37.4")])]});
            var Q1;
            Q1=qCreatedBy(makeId("Origin.pointOp"),VERTEX);
            transform(context, id + "F2", {"entities" : qUnion([Q0]), "transformType" : TransformType.SCALE_UNIFORMLY, "scale" : .95, "scalePoint" : qUnion([Q1]), "makeCopy" : false});
        }
    });
